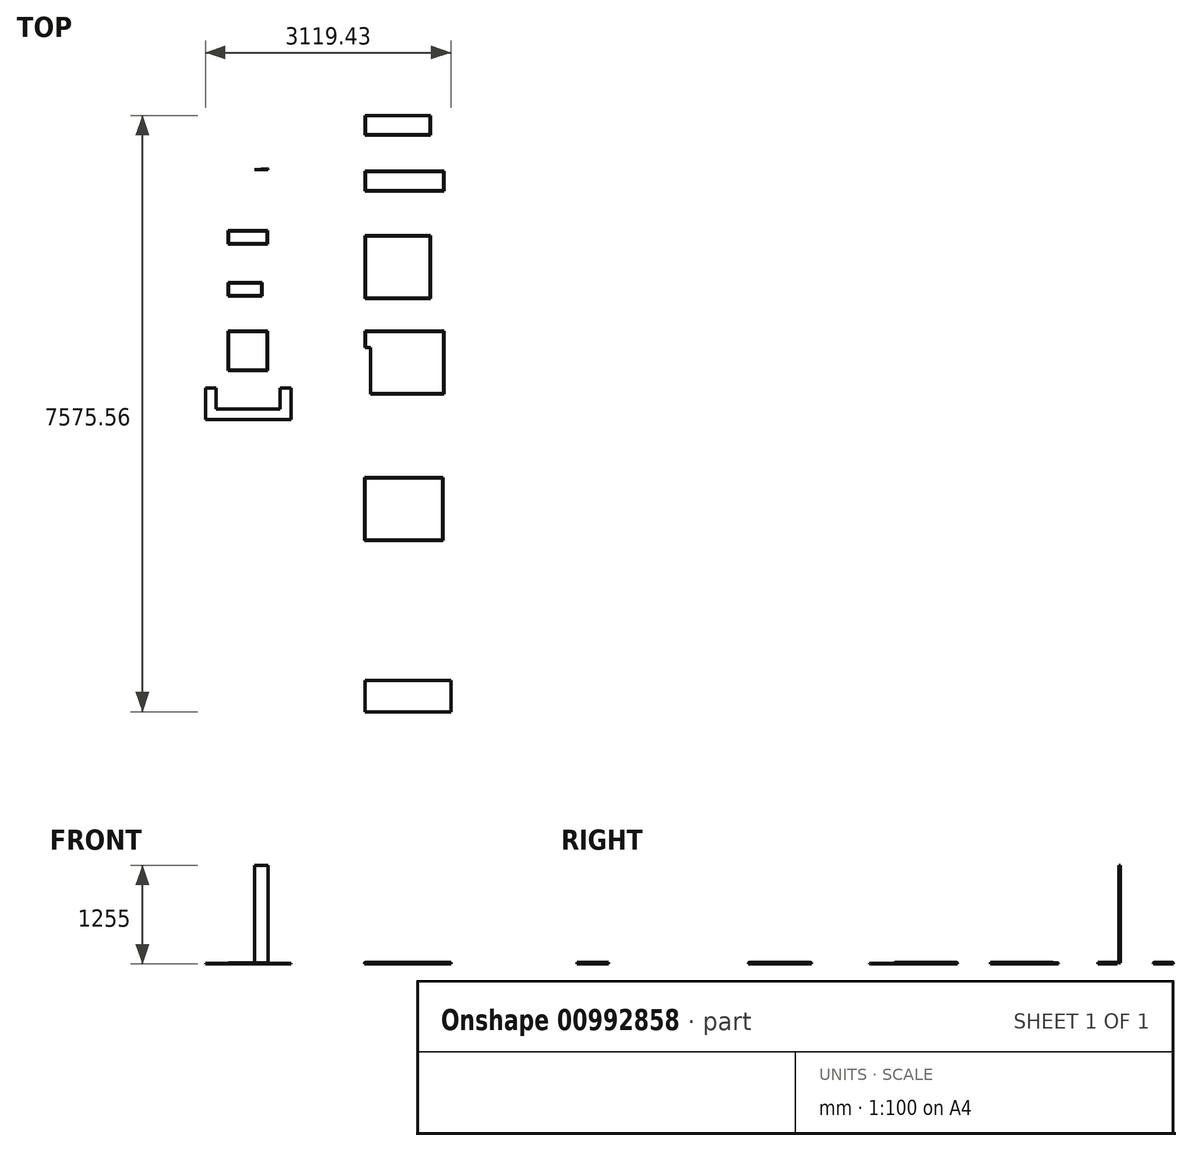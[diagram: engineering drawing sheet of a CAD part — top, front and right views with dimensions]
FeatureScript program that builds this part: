
annotation { "Feature Type Name" : "Feature", "Feature Type Description" : "" }
export const myFeature = defineFeature(function(context is Context, id is Id, definition is map)
    precondition{}
    {
        {
            var Q0;
            Q0=qCreatedBy(makeId("Top.planeOp"),FACE);
            var sketch = newSketch(context, id + "F0", { "sketchPlane" : qUnion([Q0])});
            skLineSegment(sketch, "E0.bottom", {"start": v(0, 0) * mm, "end": v(1000, 0) * mm});
            skLineSegment(sketch, "E0.top", {"start": v(66.6, -800) * mm, "end": v(1000, -800) * mm});
            skLineSegment(sketch, "E0.left", {"start": v(0, 0) * mm, "end": v(0, -210) * mm});
            skLineSegment(sketch, "E0.right", {"start": v(1000, 0) * mm, "end": v(1000, -800) * mm});
            skLineSegment(sketch, "E1", {"start": v(0, -210) * mm, "end": v(66.6, -210) * mm});
            skLineSegment(sketch, "E2", {"start": v(66.6, -800) * mm, "end": v(66.6, -210) * mm});
            skPoint(sketch, "E3.orphan", {"position": v(66.6, 0) * mm});
            skSolve(sketch);
        }
        {
            var Q0;
            Q0 = qSketchRegion(id + "F0", true);
            extrude(context, id + "F1", {"entities" : qUnion([Q0]), "depth" : 20 * mm, "offsetDistance" : 25 * mm});
        }
        {
            var Q0;
            Q0=makeQuery(id+"F1.opExtrude","CAP_EDGE",EDGE,{"disambiguationData":[OSD([sQuery(id+"F0.wireOp",EDGE,"E0.left")])],"isStart":false});
            var Q1;
            Q1=makeQuery(id+"F1.opExtrude","CAP_EDGE",EDGE,{"disambiguationData":[OSD([sQuery(id+"F0.wireOp",EDGE,"E0.bottom")])],"isStart":false});
            var Q2;
            Q2=makeQuery(id+"F1.opExtrude","CAP_EDGE",EDGE,{"disambiguationData":[OSD([sQuery(id+"F0.wireOp",EDGE,"E0.top")])],"isStart":false});
            var Q3;
            Q3=makeQuery(id+"F1.opExtrude","CAP_EDGE",EDGE,{"disambiguationData":[OSD([sQuery(id+"F0.wireOp",EDGE,"E0.right")])],"isStart":false});
            chamfer(context, id + "F2", {"entities" : qUnion([Q0, Q1, Q2, Q3]), "width" : 5 * mm, "tangentPropagation" : true});
        }
        {
            var Q0;
            Q0=makeQuery(id+"F1.opExtrude","CAP_EDGE",EDGE,{"disambiguationData":[OSD([sQuery(id+"F0.wireOp",EDGE,"E0.right")])],"isStart":true});
            var Q1;
            Q1=makeQuery(id+"F1.opExtrude","CAP_EDGE",EDGE,{"disambiguationData":[OSD([sQuery(id+"F0.wireOp",EDGE,"E0.top")])],"isStart":true});
            var Q2;
            Q2=makeQuery(id+"F1.opExtrude","CAP_EDGE",EDGE,{"disambiguationData":[OSD([sQuery(id+"F0.wireOp",EDGE,"E0.left")])],"isStart":true});
            var Q3;
            Q3=makeQuery(id+"F1.opExtrude","CAP_EDGE",EDGE,{"disambiguationData":[OSD([sQuery(id+"F0.wireOp",EDGE,"E0.bottom")])],"isStart":true});
            chamfer(context, id + "F3", {"entities" : qUnion([Q0, Q1, Q2, Q3]), "width" : 5 * mm, "tangentPropagation" : true});
        }
        {
            var Q0;
            Q0=qCreatedBy(makeId("Top.planeOp"),FACE);
            var sketch = newSketch(context, id + "F4", { "sketchPlane" : qUnion([Q0])});
            skLineSegment(sketch, "E4.bottom", {"start": v(0, 1215.82) * mm, "end": v(830, 1215.82) * mm});
            skLineSegment(sketch, "E4.top", {"start": v(0, 415.82) * mm, "end": v(830, 415.82) * mm});
            skLineSegment(sketch, "E4.left", {"start": v(0, 1215.82) * mm, "end": v(0, 415.82) * mm});
            skLineSegment(sketch, "E4.right", {"start": v(830, 1215.82) * mm, "end": v(830, 415.82) * mm});
            skSolve(sketch);
        }
        {
            var Q0;
            Q0 = qSketchRegion(id + "F4", true);
            extrude(context, id + "F5", {"entities" : qUnion([Q0]), "depth" : 20 * mm, "offsetDistance" : 25 * mm});
        }
        {
            var Q0;
            Q0=qCreatedBy(makeId("Top.planeOp"),FACE);
            var sketch = newSketch(context, id + "F6", { "sketchPlane" : qUnion([Q0])});
            skLineSegment(sketch, "E5.bottom", {"start": v(0, 2030.6) * mm, "end": v(1000, 2030.6) * mm});
            skLineSegment(sketch, "E5.top", {"start": v(0, 1780.6) * mm, "end": v(1000, 1780.6) * mm});
            skLineSegment(sketch, "E5.left", {"start": v(0, 2030.6) * mm, "end": v(0, 1780.6) * mm});
            skLineSegment(sketch, "E5.right", {"start": v(1000, 2030.6) * mm, "end": v(1000, 1780.6) * mm});
            skSolve(sketch);
        }
        {
            var Q0;
            Q0 = qSketchRegion(id + "F6", true);
            extrude(context, id + "F7", {"entities" : qUnion([Q0]), "depth" : 20 * mm, "offsetDistance" : 25 * mm});
        }
        {
            var Q0;
            Q0=makeQuery(id+"F5.opExtrude","CAP_FACE",FACE,{"disambiguationData":[OSD([sQuery(id+"F4.wireOp",EDGE,"E4.bottom"),sQuery(id+"F4.wireOp",EDGE,"E4.top"),sQuery(id+"F4.wireOp",EDGE,"E4.left"),sQuery(id+"F4.wireOp",EDGE,"E4.right")])],"isStart":false});
            chamfer(context, id + "F8", {"entities" : qUnion([Q0]), "width" : 5 * mm, "tangentPropagation" : true});
        }
        {
            var Q0;
            Q0=makeQuery(id+"F7.opExtrude","CAP_FACE",FACE,{"disambiguationData":[OSD([sQuery(id+"F6.wireOp",EDGE,"E5.bottom"),sQuery(id+"F6.wireOp",EDGE,"E5.top"),sQuery(id+"F6.wireOp",EDGE,"E5.left"),sQuery(id+"F6.wireOp",EDGE,"E5.right")])],"isStart":false});
            chamfer(context, id + "F9", {"entities" : qUnion([Q0]), "width" : 5 * mm, "tangentPropagation" : true});
        }
        {
            var Q0;
            Q0=qCreatedBy(makeId("Top.planeOp"),FACE);
            var sketch = newSketch(context, id + "F10", { "sketchPlane" : qUnion([Q0])});
            skLineSegment(sketch, "E6.bottom", {"start": v(0, 2740.7) * mm, "end": v(830, 2740.7) * mm});
            skLineSegment(sketch, "E6.top", {"start": v(0, 2490.7) * mm, "end": v(830, 2490.7) * mm});
            skLineSegment(sketch, "E6.left", {"start": v(0, 2740.7) * mm, "end": v(0, 2490.7) * mm});
            skLineSegment(sketch, "E6.right", {"start": v(830, 2740.7) * mm, "end": v(830, 2490.7) * mm});
            skSolve(sketch);
        }
        {
            var Q0;
            Q0 = qSketchRegion(id + "F10", true);
            extrude(context, id + "F11", {"entities" : qUnion([Q0]), "depth" : 20 * mm, "offsetDistance" : 25 * mm});
        }
        {
            var Q0;
            Q0=makeQuery(id+"F11.opExtrude","CAP_FACE",FACE,{"disambiguationData":[OSD([sQuery(id+"F10.wireOp",EDGE,"E6.bottom"),sQuery(id+"F10.wireOp",EDGE,"E6.top"),sQuery(id+"F10.wireOp",EDGE,"E6.left"),sQuery(id+"F10.wireOp",EDGE,"E6.right")])],"isStart":false});
            chamfer(context, id + "F12", {"entities" : qUnion([Q0]), "width" : 5 * mm, "tangentPropagation" : true});
        }
        {
            var Q0;
            Q0=qCreatedBy(makeId("Top.planeOp"),FACE);
            var sketch = newSketch(context, id + "F13", { "sketchPlane" : qUnion([Q0])});
            skLineSegment(sketch, "E7.bottom", {"start": v(-8.79, -1857.43) * mm, "end": v(991.21, -1857.43) * mm});
            skLineSegment(sketch, "E7.top", {"start": v(-8.79, -2657.43) * mm, "end": v(991.21, -2657.43) * mm});
            skLineSegment(sketch, "E7.left", {"start": v(-8.79, -1857.43) * mm, "end": v(-8.79, -2657.43) * mm});
            skLineSegment(sketch, "E7.right", {"start": v(991.21, -1857.43) * mm, "end": v(991.21, -2657.43) * mm});
            skSolve(sketch);
        }
        {
            var Q0;
            Q0 = qSketchRegion(id + "F13", true);
            extrude(context, id + "F14", {"entities" : qUnion([Q0]), "depth" : 20 * mm, "offsetDistance" : 25 * mm});
        }
        {
            var Q0;
            Q0=makeQuery(id+"F14.opExtrude","CAP_FACE",FACE,{"disambiguationData":[OSD([sQuery(id+"F13.wireOp",EDGE,"E7.bottom"),sQuery(id+"F13.wireOp",EDGE,"E7.top"),sQuery(id+"F13.wireOp",EDGE,"E7.left"),sQuery(id+"F13.wireOp",EDGE,"E7.right")])],"isStart":false});
            chamfer(context, id + "F15", {"entities" : qUnion([Q0]), "width" : 5 * mm, "tangentPropagation" : true});
        }
        {
            var Q0;
            Q0=qCreatedBy(makeId("Top.planeOp"),FACE);
            var sketch = newSketch(context, id + "F16", { "sketchPlane" : qUnion([Q0])});
            skLineSegment(sketch, "E8.bottom", {"start": v(-1740.26, 0) * mm, "end": v(-1240.26, 0) * mm});
            skLineSegment(sketch, "E8.top", {"start": v(-1740.26, -500) * mm, "end": v(-1240.26, -500) * mm});
            skLineSegment(sketch, "E8.left", {"start": v(-1740.26, 0) * mm, "end": v(-1740.26, -500) * mm});
            skLineSegment(sketch, "E8.right", {"start": v(-1240.26, 0) * mm, "end": v(-1240.26, -500) * mm});
            skLineSegment(sketch, "E9.bottom", {"start": v(-1740.26, 615.25) * mm, "end": v(-1310.26, 615.25) * mm});
            skLineSegment(sketch, "E9.top", {"start": v(-1740.26, 445.25) * mm, "end": v(-1310.26, 445.25) * mm});
            skLineSegment(sketch, "E9.left", {"start": v(-1740.26, 615.25) * mm, "end": v(-1740.26, 445.25) * mm});
            skLineSegment(sketch, "E9.right", {"start": v(-1310.26, 615.25) * mm, "end": v(-1310.26, 445.25) * mm});
            skLineSegment(sketch, "E10.bottom", {"start": v(-1740.26, 1279.68) * mm, "end": v(-1240.26, 1279.68) * mm});
            skLineSegment(sketch, "E10.top", {"start": v(-1740.26, 1109.68) * mm, "end": v(-1240.26, 1109.68) * mm});
            skLineSegment(sketch, "E10.left", {"start": v(-1740.26, 1279.68) * mm, "end": v(-1740.26, 1109.68) * mm});
            skLineSegment(sketch, "E10.right", {"start": v(-1240.26, 1279.68) * mm, "end": v(-1240.26, 1109.68) * mm});
            skSolve(sketch);
        }
        {
            var Q0;
            Q0 = qSketchRegion(id + "F16", true);
            extrude(context, id + "F17", {"entities" : qUnion([Q0]), "depth" : 15 * mm, "offsetDistance" : 25 * mm});
        }
        {
            var Q0;
            Q0=makeQuery(id+"F17.opExtrude","CAP_FACE",FACE,{"disambiguationData":[OSD([sQuery(id+"F16.wireOp",EDGE,"E8.bottom"),sQuery(id+"F16.wireOp",EDGE,"E8.top"),sQuery(id+"F16.wireOp",EDGE,"E8.left"),sQuery(id+"F16.wireOp",EDGE,"E8.right")])],"isStart":false});
            chamfer(context, id + "F18", {"entities" : qUnion([Q0]), "width" : 5 * mm, "tangentPropagation" : true});
        }
        {
            var Q0;
            Q0=makeQuery(id+"F17.opExtrude","CAP_EDGE",EDGE,{"disambiguationData":[OSD([sQuery(id+"F16.wireOp",EDGE,"E10.top")])],"isStart":false});
            var Q1;
            Q1=makeQuery(id+"F17.opExtrude","CAP_EDGE",EDGE,{"disambiguationData":[OSD([sQuery(id+"F16.wireOp",EDGE,"E10.left")])],"isStart":false});
            var Q2;
            Q2=makeQuery(id+"F17.opExtrude","CAP_EDGE",EDGE,{"disambiguationData":[OSD([sQuery(id+"F16.wireOp",EDGE,"E10.bottom")])],"isStart":false});
            var Q3;
            Q3=makeQuery(id+"F17.opExtrude","CAP_EDGE",EDGE,{"disambiguationData":[OSD([sQuery(id+"F16.wireOp",EDGE,"E10.right")])],"isStart":false});
            chamfer(context, id + "F19", {"entities" : qUnion([Q0, Q1, Q2, Q3]), "width" : 5 * mm, "tangentPropagation" : true});
        }
        {
            var Q0;
            Q0=makeQuery(id+"F17.opExtrude","CAP_EDGE",EDGE,{"disambiguationData":[OSD([sQuery(id+"F16.wireOp",EDGE,"E9.left")])],"isStart":false});
            var Q1;
            Q1=makeQuery(id+"F17.opExtrude","CAP_EDGE",EDGE,{"disambiguationData":[OSD([sQuery(id+"F16.wireOp",EDGE,"E9.bottom")])],"isStart":false});
            var Q2;
            Q2=makeQuery(id+"F17.opExtrude","CAP_EDGE",EDGE,{"disambiguationData":[OSD([sQuery(id+"F16.wireOp",EDGE,"E9.right")])],"isStart":false});
            var Q3;
            Q3=makeQuery(id+"F17.opExtrude","CAP_EDGE",EDGE,{"disambiguationData":[OSD([sQuery(id+"F16.wireOp",EDGE,"E9.top")])],"isStart":false});
            chamfer(context, id + "F20", {"entities" : qUnion([Q0, Q1, Q2, Q3]), "width" : 5 * mm, "tangentPropagation" : true});
        }
        {
            var Q0;
            Q0=makeQuery(id+"F17.opExtrude","CAP_FACE",FACE,{"disambiguationData":[OSD([sQuery(id+"F16.wireOp",EDGE,"E10.bottom"),sQuery(id+"F16.wireOp",EDGE,"E10.top"),sQuery(id+"F16.wireOp",EDGE,"E10.left"),sQuery(id+"F16.wireOp",EDGE,"E10.right")])],"isStart":false});
            var sketch = newSketch(context, id + "F21", { "sketchPlane" : qUnion([Q0])});
            skLineSegment(sketch, "E11", {"start": v(-1403.27, 2051.76) * mm, "end": v(-1233.27, 2051.76) * mm});
            skLineSegment(sketch, "E12", {"start": v(-1233.27, 2051.76) * mm, "end": v(-1233.27, 2066.76) * mm});
            skLineSegment(sketch, "E13", {"start": v(-1233.27, 2066.76) * mm, "end": v(-1403.27, 2051.76) * mm});
            skSolve(sketch);
        }
        {
            var Q0;
            Q0=makeQuery(id+"F21.imprint","IMPRINT",FACE,{"disambiguationData":[TD([[makeQuery(id+"F21.imprint","IMPRINT",EDGE,{"derivedFrom":sQuery(id+"F21.wireOp",EDGE,"E11")}),1.0]])]});
            extrude(context, id + "F22", {"entities" : qUnion([Q0]), "depth" : 1240 * mm, "offsetDistance" : 25 * mm});
        }
        {
            var Q0;
            Q0=makeQuery(id+"F22.opExtrude","SWEPT_EDGE",EDGE,{"disambiguationData":[OSD([sQuery(id+"F21.wireOp",EDGE,"E12"),sQuery(id+"F21.wireOp",EDGE,"E13")])]});
            chamfer(context, id + "F23", {"entities" : qUnion([Q0]), "width" : 5 * mm, "tangentPropagation" : true});
        }
        {
            var Q0;
            Q0=qCreatedBy(makeId("Top.planeOp"),FACE);
            var sketch = newSketch(context, id + "F24", { "sketchPlane" : qUnion([Q0])});
            skLineSegment(sketch, "E14.bottom", {"start": v(-2029.43, -721) * mm, "end": v(-1895.43, -721) * mm});
            skLineSegment(sketch, "E14.top", {"start": v(-2029.43, -1121) * mm, "end": v(-942.43, -1121) * mm});
            skLineSegment(sketch, "E14.left", {"start": v(-2029.43, -721) * mm, "end": v(-2029.43, -1121) * mm});
            skLineSegment(sketch, "E14.right", {"start": v(-942.43, -721) * mm, "end": v(-942.43, -1121) * mm});
            skLineSegment(sketch, "E15", {"start": v(-1895.43, -721) * mm, "end": v(-1895.43, -987) * mm});
            skLineSegment(sketch, "E16", {"start": v(-1895.43, -987) * mm, "end": v(-1082.43, -987) * mm});
            skLineSegment(sketch, "E17", {"start": v(-1082.43, -987) * mm, "end": v(-1082.43, -721) * mm});
            skLineSegment(sketch, "E18.trimOffspring", {"start": v(-1082.43, -721) * mm, "end": v(-942.43, -721) * mm});
            skSolve(sketch);
        }
        {
            var Q0;
            Q0=makeQuery(id+"F24.imprint","IMPRINT",FACE,{"disambiguationData":[TD([[makeQuery(id+"F24.imprint","IMPRINT",EDGE,{"derivedFrom":sQuery(id+"F24.wireOp",EDGE,"E14.bottom")}),-1.0]])]});
            extrude(context, id + "F25", {"entities" : qUnion([Q0]), "depth" : 10 * mm, "offsetDistance" : 25 * mm});
        }
        {
            var Q0;
            Q0=qCreatedBy(makeId("Top.planeOp"),FACE);
            var sketch = newSketch(context, id + "F26", { "sketchPlane" : qUnion([Q0])});
            skLineSegment(sketch, "E19.bottom", {"start": v(0, -4434.86) * mm, "end": v(1090, -4434.86) * mm});
            skLineSegment(sketch, "E19.top", {"start": v(0, -4834.86) * mm, "end": v(1090, -4834.86) * mm});
            skLineSegment(sketch, "E19.left", {"start": v(0, -4434.86) * mm, "end": v(0, -4834.86) * mm});
            skLineSegment(sketch, "E19.right", {"start": v(1090, -4434.86) * mm, "end": v(1090, -4834.86) * mm});
            skSolve(sketch);
        }
        {
            var Q0;
            Q0=makeQuery(id+"F26.imprint","IMPRINT",FACE,{"disambiguationData":[TD([[makeQuery(id+"F26.imprint","IMPRINT",EDGE,{"derivedFrom":sQuery(id+"F26.wireOp",EDGE,"E19.bottom")}),-1.0]])]});
            extrude(context, id + "F27", {"entities" : qUnion([Q0]), "depth" : 20 * mm, "offsetDistance" : 25 * mm});
        }
    });
